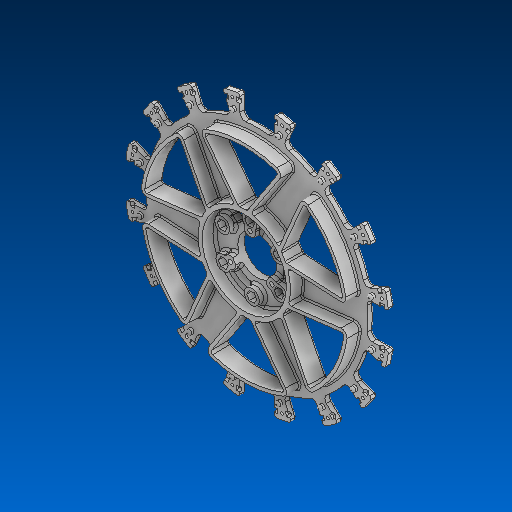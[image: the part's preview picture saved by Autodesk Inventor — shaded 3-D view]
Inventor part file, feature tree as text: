
AUTODESK INVENTOR PART (.ipt)
format: ipt  version: 2022.2 (Build 262287000, 287)  size: 1,838,592 bytes
history: native  units: in
note: dims shown in document units (in); Inventor stores cm internally (conversion verified against a paired STEP export)
features: fillet x1
ambient origin geometry x8: Origin, YZ Plane, XZ Plane, XY Plane, X Axis, Y Axis, Z Axis, Center Point
bodies: Solid1 (feature_tree)
feature tree (1):
  fillet  "Fillet16"  [1 undecoded]
note: 1 required parameter value undecoded (feature->parameter linkage not recoverable at this tier; creation-order binding heuristic only, values carry confidence <= 0.55)
